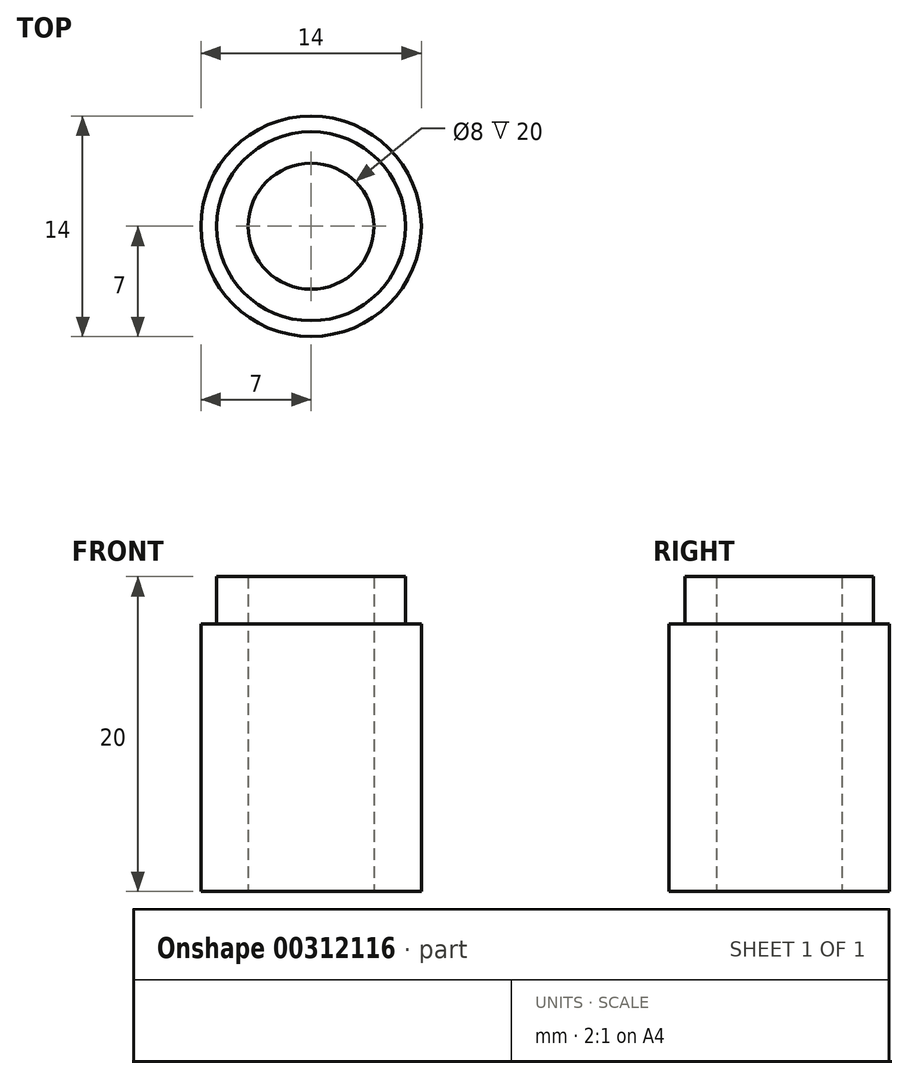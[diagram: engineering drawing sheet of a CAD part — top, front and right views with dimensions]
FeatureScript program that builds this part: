
annotation { "Feature Type Name" : "Feature", "Feature Type Description" : "" }
export const myFeature = defineFeature(function(context is Context, id is Id, definition is map)
    precondition{}
    {
        {
            var Q0;
            Q0=qCreatedBy(makeId("Front.planeOp"),FACE);
            var sketch = newSketch(context, id + "F0", { "sketchPlane" : qUnion([Q0])});
            skLineSegment(sketch, "E0", {"start": v(0, 0) * mm, "end": v(0, 14.25) * mm, "construction": true});
            skLineSegment(sketch, "E1", {"start": v(4, 0) * mm, "end": v(4, 20) * mm});
            skLineSegment(sketch, "E2", {"start": v(4, 20) * mm, "end": v(6, 20) * mm});
            skLineSegment(sketch, "E3", {"start": v(6, 20) * mm, "end": v(6, 17) * mm});
            skLineSegment(sketch, "E4", {"start": v(6, 17) * mm, "end": v(7, 17) * mm});
            skLineSegment(sketch, "E5", {"start": v(7, 17) * mm, "end": v(7, 0) * mm});
            skLineSegment(sketch, "E6", {"start": v(7, 0) * mm, "end": v(4, 0) * mm});
            skSolve(sketch);
        }
        {
            var Q0;
            Q0 = qSketchRegion(id + "F0", true);
            var Q1;
            Q1=sQuery(id+"F0.wireOp",EDGE,"E0");
            revolve(context, id + "F1", {"entities" : qUnion([Q0]), "axis" : qUnion([Q1]), "revolveType" : RevolveType.FULL});
        }
    });
